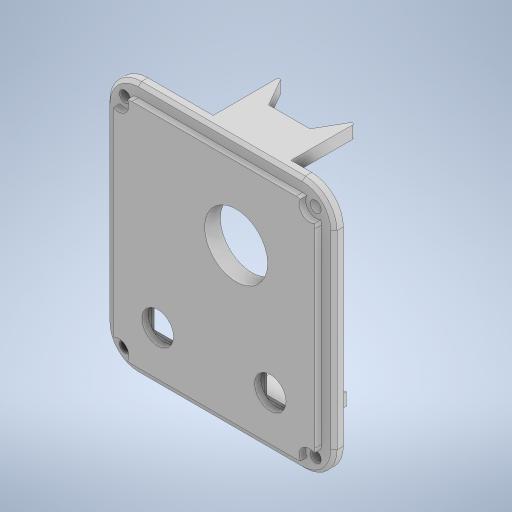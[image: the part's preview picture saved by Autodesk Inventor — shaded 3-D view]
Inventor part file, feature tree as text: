
AUTODESK INVENTOR PART (.ipt)
format: ipt  version: 2023 (Build 270158000, 158)  size: 421,376 bytes
history: native  units: mm
features: extrude x10, sketch x7, projected_geometry x3, fillet x2, other x1, chamfer x1
ambient origin geometry x8: Origin, YZ Plane, XZ Plane, XY Plane, X Axis, Y Axis, Z Axis, Center Point
bodies: Body1 (feature_tree)
feature tree (24):
  other  "솔리드1"
  sketch  "스케치1"
  extrude  "돌출1"  Depth=72.0mm
  extrude  "돌출2"  Depth=80.2mm
  extrude  "돌출3"  Depth=10.0mm
  extrude  "돌출5"  Depth=4.0mm
  fillet  "모깎기1"  Radius=3.5mm
  extrude  "돌출6"  Depth=6.5mm
  extrude  "돌출7"  Depth=3.0mm TaperAngle=0.0deg
  fillet  "모깎기2"  Radius=41.3mm
  extrude  "돌출8"  Depth=2.0mm TaperAngle=0.0deg
  chamfer  "모따기1"  Distance=10.0mm
  extrude  "돌출10"  Depth=27.0mm TaperAngle=0.0deg
  extrude  "돌출11"  Depth=25.0mm
  extrude  "돌출12"  Depth=1.0mm
  sketch  "스케치3"
  projected_geometry  "투영된 루프1"
  sketch  "스케치5"
  sketch  "스케치6"
  sketch  "스케치8"
  sketch  "스케치9"
  projected_geometry  "투영된 루프3"
  projected_geometry  "투영된 루프4"
  sketch  "스케치10"
